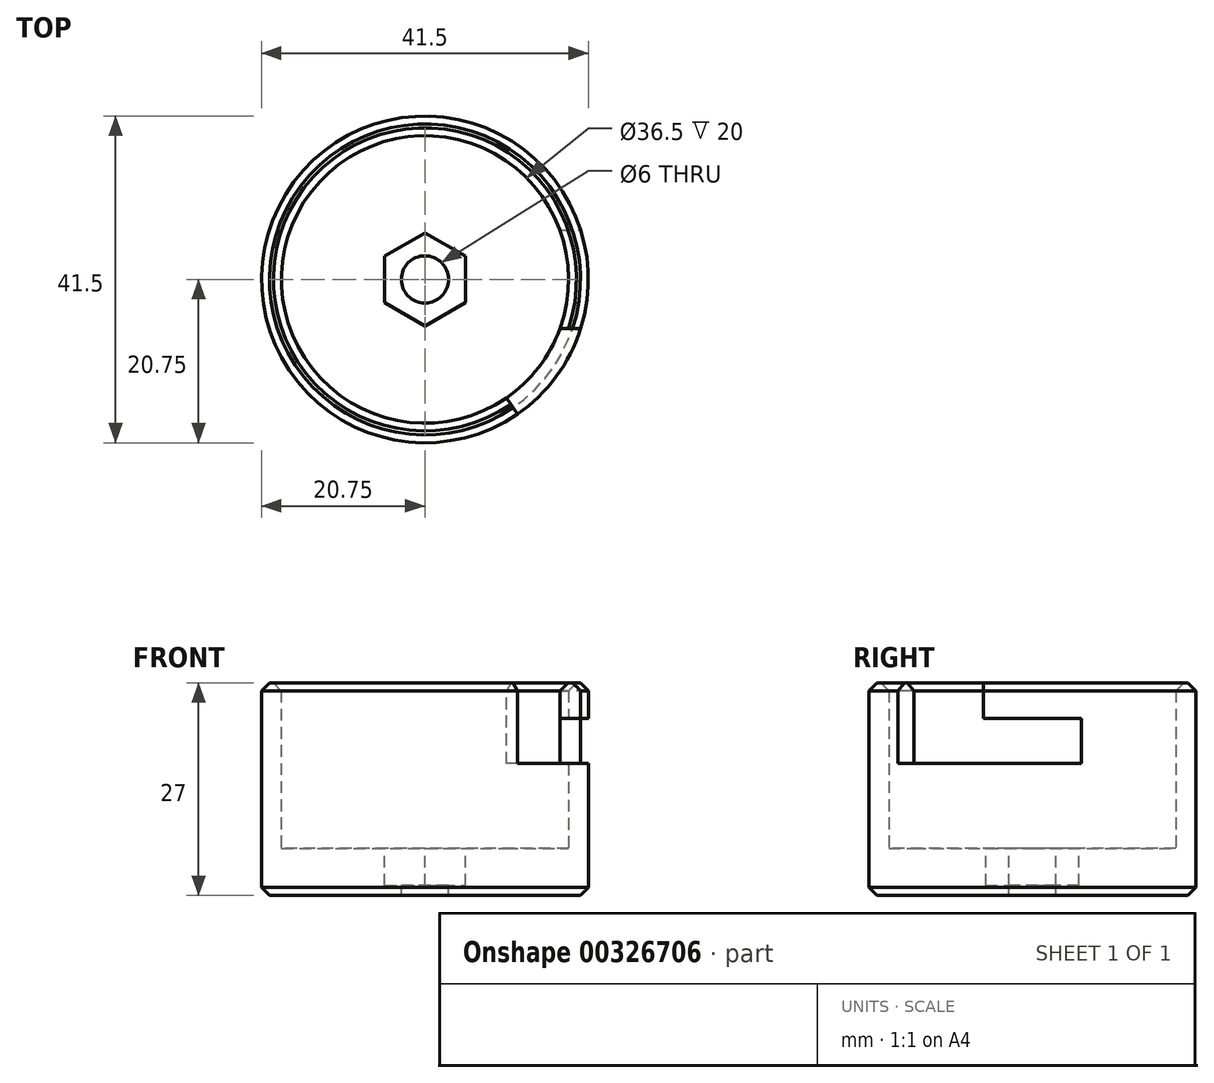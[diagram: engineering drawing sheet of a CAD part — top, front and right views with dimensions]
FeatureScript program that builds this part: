
annotation { "Feature Type Name" : "Feature", "Feature Type Description" : "" }
export const myFeature = defineFeature(function(context is Context, id is Id, definition is map)
    precondition{}
    {
        {
            var Q0;
            Q0=qCreatedBy(makeId("Top.planeOp"),FACE);
            var sketch = newSketch(context, id + "F0", { "sketchPlane" : qUnion([Q0])});
            skCircle(sketch, "E0", {"center": v(0, 0) * mm, "radius": 20.75 * mm});
            skSolve(sketch);
        }
        {
            var Q0;
            Q0=makeQuery(id+"F0.imprint","IMPRINT",FACE,{"disambiguationData":[TD([[makeQuery(id+"F0.imprint","IMPRINT",EDGE,{"derivedFrom":sQuery(id+"F0.wireOp",EDGE,"E0")}),1.0]])]});
            extrude(context, id + "F1", {"entities" : qUnion([Q0]), "depth" : 6 * mm});
        }
        {
            var Q0;
            Q0=makeQuery(id+"F1.opExtrude","CAP_FACE",FACE,{"disambiguationData":[OSD([sQuery(id+"F0.wireOp",EDGE,"E0")])],"isStart":false});
            var sketch = newSketch(context, id + "F2", { "sketchPlane" : qUnion([Q0])});
            skCircle(sketch, "E1.cCircle", {"center": v(0, 0) * mm, "radius": 5.12 * mm, "construction": true});
            skLineSegment(sketch, "E1.0", {"start": v(5.12, 2.96) * mm, "end": v(5.12, -2.96) * mm});
            skLineSegment(sketch, "E1.1", {"start": v(5.13, -2.96) * mm, "end": v(0, -5.92) * mm});
            skLineSegment(sketch, "E1.2", {"start": v(0, -5.92) * mm, "end": v(-5.12, -2.96) * mm});
            skLineSegment(sketch, "E1.3", {"start": v(-5.12, -2.96) * mm, "end": v(-5.13, 2.96) * mm});
            skLineSegment(sketch, "E1.4", {"start": v(-5.13, 2.96) * mm, "end": v(0, 5.92) * mm});
            skLineSegment(sketch, "E1.5", {"start": v(0, 5.92) * mm, "end": v(5.13, 2.96) * mm});
            skPoint(sketch, "E1.0.midPoint", {"position": v(5.12, 0) * mm});
            skSolve(sketch);
        }
        {
            var Q0;
            Q0=makeQuery(id+"F2.imprint","IMPRINT",FACE,{"disambiguationData":[TD([[makeQuery(id+"F2.imprint","IMPRINT",EDGE,{"derivedFrom":sQuery(id+"F2.wireOp",EDGE,"E1.0")}),-1.0]])]});
            extrude(context, id + "F3", {"entities" : qUnion([Q0]), "operationType" : NewBodyOperationType.REMOVE, "oppositeDirection" : true, "depth" : 4.75 * mm});
        }
        {
            var Q0;
            Q0=makeQuery(id+"F3.boolean.opBoolean","COPY",FACE,{"derivedFrom":makeQuery(id+"F3.opExtrude","CAP_FACE",FACE,{"disambiguationData":[OSD([sQuery(id+"F2.wireOp",EDGE,"E1.0"),sQuery(id+"F2.wireOp",EDGE,"E1.1"),sQuery(id+"F2.wireOp",EDGE,"E1.2"),sQuery(id+"F2.wireOp",EDGE,"E1.3"),sQuery(id+"F2.wireOp",EDGE,"E1.4"),sQuery(id+"F2.wireOp",EDGE,"E1.5")])],"isStart":false})});
            var sketch = newSketch(context, id + "F4", { "sketchPlane" : qUnion([Q0])});
            skCircle(sketch, "E2", {"center": v(0, 0) * mm, "radius": 3 * mm});
            skSolve(sketch);
        }
        {
            var Q0;
            Q0=makeQuery(id+"F4.imprint","IMPRINT",FACE,{"disambiguationData":[TD([[makeQuery(id+"F4.imprint","IMPRINT",EDGE,{"derivedFrom":sQuery(id+"F4.wireOp",EDGE,"E2")}),1.0]])]});
            extrude(context, id + "F5", {"entities" : qUnion([Q0]), "operationType" : NewBodyOperationType.REMOVE, "endBound" : BoundingType.UP_TO_NEXT, "oppositeDirection" : true, "depth" : 25 * mm});
        }
        {
            var Q0;
            Q0=makeQuery(id+"F1.opExtrude","CAP_FACE",FACE,{"disambiguationData":[OSD([sQuery(id+"F0.wireOp",EDGE,"E0")])],"isStart":false});
            var sketch = newSketch(context, id + "F6", { "sketchPlane" : qUnion([Q0])});
            skCircle(sketch, "E3.0", {"center": v(0, 0) * mm, "radius": 20.75 * mm});
            skCircle(sketch, "E4", {"center": v(0, 0) * mm, "radius": 18.25 * mm});
            skSolve(sketch);
        }
        {
            var Q0;
            Q0=makeQuery(id+"F6.imprint","IMPRINT",FACE,{"disambiguationData":[TD([[makeQuery(id+"F6.imprint","IMPRINT",EDGE,{"derivedFrom":sQuery(id+"F6.wireOp",EDGE,"E3.0")}),1.0]])]});
            extrude(context, id + "F7", {"entities" : qUnion([Q0]), "operationType" : NewBodyOperationType.ADD, "depth" : 21 * mm});
        }
        {
            var Q0;
            Q0=qCreatedBy(makeId("Right.planeOp"),FACE);
            cPlane(context, id + "F8", {"entities" : qUnion([Q0]), "cplaneType" : CPlaneType.OFFSET, "offset" : (41.5 / 2) * mm, "width" : 150 * mm, "height" : 150 * mm});
        }
        {
            var Q0;
            Q0=qCreatedBy(id+"F8.planeOp",FACE);
            var sketch = newSketch(context, id + "F9", { "sketchPlane" : qUnion([Q0])});
            skLineSegment(sketch, "E5.0", {"start": v(-20.75, 27) * mm, "end": v(20.75, 27) * mm});
            skLineSegment(sketch, "E6", {"start": v(-20.75, 0) * mm, "end": v(-20.75, 27) * mm});
            skLineSegment(sketch, "E7", {"start": v(20.75, 27) * mm, "end": v(20.75, 0) * mm});
            skLineSegment(sketch, "E8.bottom", {"start": v(-6.25, 22.5) * mm, "end": v(6.25, 22.5) * mm});
            skLineSegment(sketch, "E8.top", {"start": v(-6.25, 16.75) * mm, "end": v(6.25, 16.75) * mm});
            skLineSegment(sketch, "E8.left", {"start": v(-6.25, 22.5) * mm, "end": v(-6.25, 16.75) * mm});
            skLineSegment(sketch, "E8.right", {"start": v(6.25, 22.5) * mm, "end": v(6.25, 16.75) * mm});
            skLineSegment(sketch, "E9", {"start": v(0, 0) * mm, "end": v(0, 31.74) * mm, "construction": true});
            skSolve(sketch);
        }
        {
            var Q0;
            Q0=makeQuery(id+"F9.imprint","IMPRINT",FACE,{"disambiguationData":[TD([[makeQuery(id+"F9.imprint","IMPRINT",EDGE,{"derivedFrom":sQuery(id+"F9.wireOp",EDGE,"E8.bottom")}),-1.0]])]});
            var Q1;
            Q1=makeQuery(id+"F7.opExtrude","SWEPT_FACE",FACE,{"disambiguationData":[OSD([sQuery(id+"F6.wireOp",EDGE,"E4")])]});
            extrude(context, id + "F10", {"entities" : qUnion([Q0]), "operationType" : NewBodyOperationType.REMOVE, "endBound" : BoundingType.UP_TO_SURFACE, "oppositeDirection" : true, "endBoundEntityFace" : qUnion([Q1]), "depth" : 25 * mm});
        }
        {
            var Q0;
            Q0=makeQuery(id+"F7.opExtrude","CAP_FACE",FACE,{"disambiguationData":[OSD([sQuery(id+"F6.wireOp",EDGE,"E3.0"),sQuery(id+"F6.wireOp",EDGE,"E4")])],"isStart":false});
            var sketch = newSketch(context, id + "F11", { "sketchPlane" : qUnion([Q0])});
            skArc(sketch, "E10.0", {"start": v(19.79, 6.25) * mm, "mid": v(20.75, 0) * mm, "end": v(19.79, -6.25) * mm});
            skArc(sketch, "E11.0", {"start": v(17.15, -6.25) * mm, "mid": v(18.25, 0) * mm, "end": v(17.15, 6.25) * mm});
            skLineSegment(sketch, "E12.0", {"start": v(17.15, -6.25) * mm, "end": v(19.79, -6.25) * mm});
            skPoint(sketch, "E13.0", {"position": v(18.47, 6.25) * mm});
            skLineSegment(sketch, "E14.0", {"start": v(17.15, 6.25) * mm, "end": v(19.79, 6.25) * mm});
            skCircle(sketch, "E15.0.0", {"center": v(0, 0) * mm, "radius": 20.75 * mm});
            skCircle(sketch, "E16.0", {"center": v(0, 0) * mm, "radius": 18.25 * mm});
            skLineSegment(sketch, "E17", {"start": v(0, 0) * mm, "end": v(11.75, -17.1) * mm, "construction": true});
            skLineSegment(sketch, "E18", {"start": v(11.75, -17.1) * mm, "end": v(10.34, -15.04) * mm});
            skSolve(sketch);
        }
        {
            var Q0;
            {var subQ0=sQuery(id+"F11.wireOp",EDGE,"E12.0");Q0=makeQuery(id+"F11.imprint","IMPRINT",FACE,{"disambiguationData":[TD([[makeQuery(id+"F11.imprint","IMPRINT",EDGE,{"derivedFrom":subQ0}),-1.0]])]});}
            var Q1;
            Q1=makeQuery(id+"F10.boolean.opBoolean","COPY",FACE,{"derivedFrom":makeQuery(id+"F10.opExtrude","SWEPT_FACE",FACE,{"disambiguationData":[OSD([sQuery(id+"F9.wireOp",EDGE,"E8.top")])]})});
            extrude(context, id + "F12", {"entities" : qUnion([Q0]), "operationType" : NewBodyOperationType.REMOVE, "endBound" : BoundingType.UP_TO_SURFACE, "oppositeDirection" : true, "endBoundEntityFace" : qUnion([Q1]), "depth" : 25 * mm});
        }
        {
            var Q0;
            Q0=makeQuery(id+"F7.opExtrude","CAP_EDGE",EDGE,{"disambiguationData":[OSD([sQuery(id+"F6.wireOp",EDGE,"E3.0")])],"isStart":false});
            var Q1;
            Q1=makeQuery(id+"F7.opExtrude","CAP_EDGE",EDGE,{"disambiguationData":[OSD([sQuery(id+"F6.wireOp",EDGE,"E4")])],"isStart":false});
            var Q2;
            Q2=makeQuery(id+"F1.opExtrude","CAP_EDGE",EDGE,{"disambiguationData":[OSD([sQuery(id+"F0.wireOp",EDGE,"E0")])],"isStart":true});
            chamfer(context, id + "F13", {"entities" : qUnion([Q0, Q1, Q2]), "width" : 1 * mm, "tangentPropagation" : true});
        }
    });
